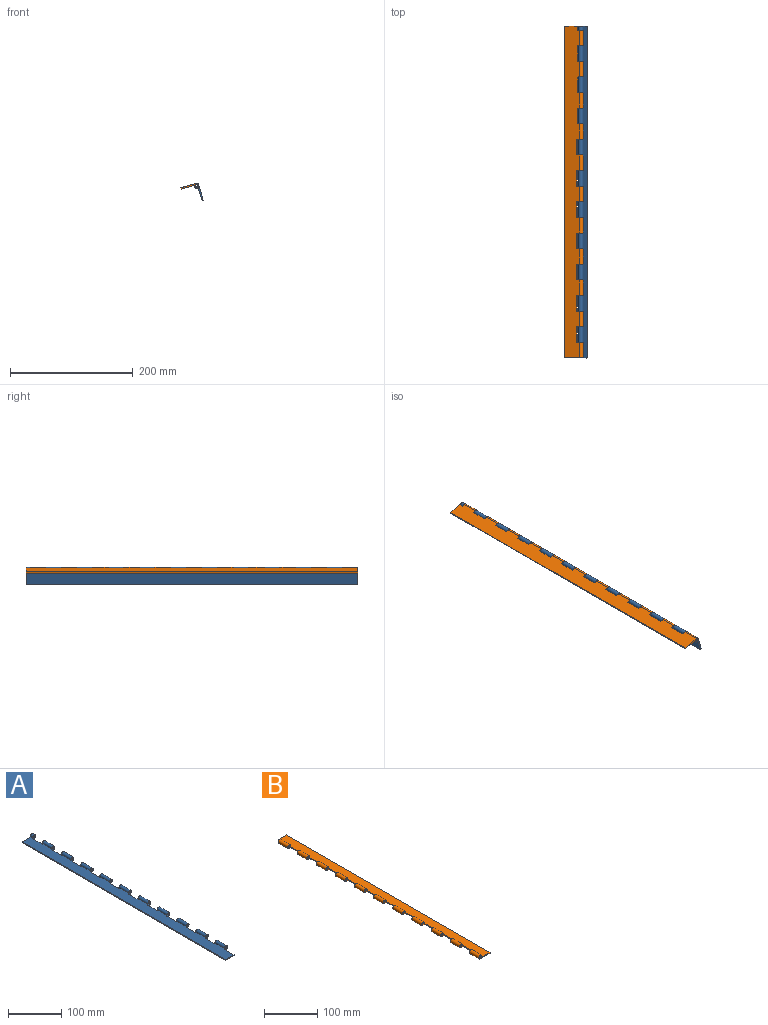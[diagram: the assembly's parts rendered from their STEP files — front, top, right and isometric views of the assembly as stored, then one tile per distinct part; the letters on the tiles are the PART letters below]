
ASSEMBLY  parts=2 mates=1
PART A: 71 faces, bbox 29.5x540x8 mm
  f0: plane 540x25.5mm, normal (0,0,1), area 12652.4mm2, adj f13,f14,f15,f16,f17,f18,f19,f20
  f1: plane 540x25.5mm, normal (0,0,-1), area 12652.4mm2, adj f24,f25,f26,f27,f28,f29,f30,f31
  f2: plane 6.6x2mm, normal (0,0,-1), area 13.2mm2, adj f13,f24,f38,f68
  f3: plane 25.4x2mm, normal (0,0,-1), area 50.8mm2, adj f14,f25,f66,f70
  f4: plane 25.4x2mm, normal (0,0,-1), area 50.8mm2, adj f15,f26,f63,f65
  f5: plane 25.4x2mm, normal (0,0,-1), area 50.8mm2, adj f16,f27,f60,f62
  f6: plane 25.4x2mm, normal (0,0,-1), area 50.8mm2, adj f17,f28,f57,f59
  f7: plane 25.4x2mm, normal (0,0,-1), area 50.8mm2, adj f18,f29,f54,f56
  f8: plane 25.4x2mm, normal (0,0,-1), area 50.8mm2, adj f19,f30,f48,f50
  f9: plane 25.4x2mm, normal (0,0,-1), area 50.8mm2, adj f20,f31,f51,f53
  f10: plane 25.4x2mm, normal (0,0,-1), area 50.8mm2, adj f21,f32,f45,f47
  f11: plane 25.4x2mm, normal (0,0,-1), area 50.8mm2, adj f22,f33,f42,f44
  f12: plane 25.4x2mm, normal (0,0,-1), area 50.8mm2, adj f23,f34,f39,f41
  f13: cylinder r=2mm len=6.6mm, axis (0,1,0), area 62.2mm2, adj f0,f2,f38,f68
  f14: cylinder r=2mm len=25.4mm, axis (0,1,0), area 239.4mm2, adj f0,f3,f66,f70
  f15: cylinder r=2mm len=25.4mm, axis (0,1,0), area 239.4mm2, adj f0,f4,f63,f65
  f16: cylinder r=2mm len=25.4mm, axis (0,1,0), area 239.4mm2, adj f0,f5,f60,f62
  f17: cylinder r=2mm len=25.4mm, axis (0,1,0), area 239.4mm2, adj f0,f6,f57,f59
  f18: cylinder r=2mm len=25.4mm, axis (0,1,0), area 239.4mm2, adj f0,f7,f54,f56
  f19: cylinder r=2mm len=25.4mm, axis (0,1,0), area 239.4mm2, adj f0,f8,f48,f50
  f20: cylinder r=2mm len=25.4mm, axis (0,1,0), area 239.4mm2, adj f0,f9,f51,f53
  f21: cylinder r=2mm len=25.4mm, axis (0,1,0), area 239.4mm2, adj f0,f10,f45,f47
  f22: cylinder r=2mm len=25.4mm, axis (0,1,0), area 239.4mm2, adj f0,f11,f42,f44
  f23: cylinder r=2mm len=25.4mm, axis (0,1,0), area 239.4mm2, adj f0,f12,f39,f41
  f24: cylinder r=4mm len=8mm, axis (0,1,0), area 124.4mm2, adj f1,f2,f38,f68
  f25: cylinder r=4mm len=25.4mm, axis (0,1,0), area 478.8mm2, adj f1,f3,f66,f70
  f26: cylinder r=4mm len=25.4mm, axis (0,1,0), area 478.8mm2, adj f1,f4,f63,f65
  f27: cylinder r=4mm len=25.4mm, axis (0,1,0), area 478.8mm2, adj f1,f5,f60,f62
  f28: cylinder r=4mm len=25.4mm, axis (0,1,0), area 478.8mm2, adj f1,f6,f57,f59
  f29: cylinder r=4mm len=25.4mm, axis (0,1,0), area 478.8mm2, adj f1,f7,f54,f56
  f30: cylinder r=4mm len=25.4mm, axis (0,1,0), area 478.8mm2, adj f1,f8,f48,f50
  f31: cylinder r=4mm len=25.4mm, axis (0,1,0), area 478.8mm2, adj f1,f9,f51,f53
  f32: cylinder r=4mm len=25.4mm, axis (0,1,0), area 478.8mm2, adj f1,f10,f45,f47
  f33: cylinder r=4mm len=25.4mm, axis (0,1,0), area 478.8mm2, adj f1,f11,f42,f44
  f34: cylinder r=4mm len=25.4mm, axis (0,1,0), area 478.8mm2, adj f1,f12,f39,f41
  f35: plane 21.5x2mm, normal (0,-1,0), area 43mm2, adj f0,f1,f37,f40
  f36: plane 25.5x2mm, normal (0,1,0), area 51mm2, adj f0,f1,f37,f38
  f37: plane 540x2mm, normal (-1,0,0), area 1080mm2, adj f0,f1,f35,f36
  f38: plane 8x8mm, normal (0,1,0), area 28.3mm2, adj f2,f13,f24,f36
  f39: plane 8x8mm, normal (0,-1,0), area 36.3mm2, adj f0,f1,f12,f23,f34,f40
  f40: plane 25.4x2mm, normal (1,0,0), area 50.8mm2, adj f0,f1,f35,f39
  f41: plane 8x8mm, normal (0,1,0), area 36.3mm2, adj f0,f1,f12,f23,f34,f43
  f42: plane 8x8mm, normal (0,-1,0), area 36.3mm2, adj f0,f1,f11,f22,f33,f43
  f43: plane 25.4x2mm, normal (1,0,0), area 50.8mm2, adj f0,f1,f41,f42
  f44: plane 8x8mm, normal (0,1,0), area 36.3mm2, adj f0,f1,f11,f22,f33,f46
  f45: plane 8x8mm, normal (0,-1,0), area 36.3mm2, adj f0,f1,f10,f21,f32,f46
  f46: plane 25.4x2mm, normal (1,0,0), area 50.8mm2, adj f0,f1,f44,f45
  f47: plane 8x8mm, normal (0,1,0), area 36.3mm2, adj f0,f1,f10,f21,f32,f49
  f48: plane 8x8mm, normal (0,-1,0), area 36.3mm2, adj f0,f1,f8,f19,f30,f49
  f49: plane 25.4x2mm, normal (1,0,0), area 50.8mm2, adj f0,f1,f47,f48
  f50: plane 8x8mm, normal (0,1,0), area 36.3mm2, adj f0,f1,f8,f19,f30,f52
  f51: plane 8x8mm, normal (0,-1,0), area 36.3mm2, adj f0,f1,f9,f20,f31,f52
  f52: plane 25.4x2mm, normal (1,0,0), area 50.8mm2, adj f0,f1,f50,f51
  f53: plane 8x8mm, normal (0,1,0), area 36.3mm2, adj f0,f1,f9,f20,f31,f55
  f54: plane 8x8mm, normal (0,-1,0), area 36.3mm2, adj f0,f1,f7,f18,f29,f55
  f55: plane 25.4x2mm, normal (1,0,0), area 50.8mm2, adj f0,f1,f53,f54
  f56: plane 8x8mm, normal (0,1,0), area 36.3mm2, adj f0,f1,f7,f18,f29,f58
  f57: plane 8x8mm, normal (0,-1,0), area 36.3mm2, adj f0,f1,f6,f17,f28,f58
  f58: plane 25.4x2mm, normal (1,0,0), area 50.8mm2, adj f0,f1,f56,f57
  f59: plane 8x8mm, normal (0,1,0), area 36.3mm2, adj f0,f1,f6,f17,f28,f61
  f60: plane 8x8mm, normal (0,-1,0), area 36.3mm2, adj f0,f1,f5,f16,f27,f61
  f61: plane 25.4x2mm, normal (1,0,0), area 50.8mm2, adj f0,f1,f59,f60
  f62: plane 8x8mm, normal (0,1,0), area 36.3mm2, adj f0,f1,f5,f16,f27,f64
  f63: plane 8x8mm, normal (0,-1,0), area 36.3mm2, adj f0,f1,f4,f15,f26,f64
  f64: plane 25.4x2mm, normal (1,0,0), area 50.8mm2, adj f0,f1,f62,f63
  f65: plane 8x8mm, normal (0,1,0), area 36.3mm2, adj f0,f1,f4,f15,f26,f67
  f66: plane 8x8mm, normal (0,-1,0), area 36.3mm2, adj f0,f1,f3,f14,f25,f67
  f67: plane 25.4x2mm, normal (1,0,0), area 50.8mm2, adj f0,f1,f65,f66
  f68: plane 8x8mm, normal (0,-1,0), area 36.3mm2, adj f0,f1,f2,f13,f24,f69
  f69: plane 25.4x2mm, normal (1,0,0), area 50.8mm2, adj f0,f1,f68,f70
  f70: plane 8x8mm, normal (0,1,0), area 36.3mm2, adj f0,f1,f3,f14,f25,f69
PART B: 71 faces, bbox 29.5x540x8 mm
  f0: plane 540x25.5mm, normal (0,0,1), area 12489.5mm2, adj f13,f14,f15,f16,f17,f18,f19,f20
  f1: plane 540x25.5mm, normal (0,0,-1), area 12489.5mm2, adj f24,f25,f26,f27,f28,f29,f30,f31
  f2: plane 25.4x2mm, normal (0,0,-1), area 50.8mm2, adj f13,f24,f40,f69
  f3: plane 25.4x2mm, normal (0,0,-1), area 50.8mm2, adj f14,f25,f65,f70
  f4: plane 25.4x2mm, normal (0,0,-1), area 50.8mm2, adj f15,f26,f62,f66
  f5: plane 25.4x2mm, normal (0,0,-1), area 50.8mm2, adj f16,f27,f59,f63
  f6: plane 25.4x2mm, normal (0,0,-1), area 50.8mm2, adj f17,f28,f56,f60
  f7: plane 25.4x2mm, normal (0,0,-1), area 50.8mm2, adj f18,f29,f53,f57
  f8: plane 25.4x2mm, normal (0,0,-1), area 50.8mm2, adj f19,f30,f50,f54
  f9: plane 25.4x2mm, normal (0,0,-1), area 50.8mm2, adj f20,f31,f47,f51
  f10: plane 25.4x2mm, normal (0,0,-1), area 50.8mm2, adj f21,f32,f44,f48
  f11: plane 25.4x2mm, normal (0,0,-1), area 50.8mm2, adj f22,f33,f42,f45
  f12: plane 25.4x2mm, normal (0,0,-1), area 50.8mm2, adj f23,f34,f38,f39
  f13: cylinder r=2mm len=25.4mm, axis (0,1,0), area 239.4mm2, adj f0,f2,f40,f69
  f14: cylinder r=2mm len=25.4mm, axis (0,1,0), area 239.4mm2, adj f0,f3,f65,f70
  f15: cylinder r=2mm len=25.4mm, axis (0,1,0), area 239.4mm2, adj f0,f4,f62,f66
  f16: cylinder r=2mm len=25.4mm, axis (0,1,0), area 239.4mm2, adj f0,f5,f59,f63
  f17: cylinder r=2mm len=25.4mm, axis (0,1,0), area 239.4mm2, adj f0,f6,f56,f60
  f18: cylinder r=2mm len=25.4mm, axis (0,1,0), area 239.4mm2, adj f0,f7,f53,f57
  f19: cylinder r=2mm len=25.4mm, axis (0,1,0), area 239.4mm2, adj f0,f8,f50,f54
  f20: cylinder r=2mm len=25.4mm, axis (0,1,0), area 239.4mm2, adj f0,f9,f47,f51
  f21: cylinder r=2mm len=25.4mm, axis (0,1,0), area 239.4mm2, adj f0,f10,f44,f48
  f22: cylinder r=2mm len=25.4mm, axis (0,1,0), area 239.4mm2, adj f0,f11,f42,f45
  f23: cylinder r=2mm len=25.4mm, axis (0,1,0), area 239.4mm2, adj f0,f12,f38,f39
  f24: cylinder r=4mm len=25.4mm, axis (0,1,0), area 478.8mm2, adj f1,f2,f40,f69
  f25: cylinder r=4mm len=25.4mm, axis (0,1,0), area 478.8mm2, adj f1,f3,f65,f70
  f26: cylinder r=4mm len=25.4mm, axis (0,1,0), area 478.8mm2, adj f1,f4,f62,f66
  f27: cylinder r=4mm len=25.4mm, axis (0,1,0), area 478.8mm2, adj f1,f5,f59,f63
  f28: cylinder r=4mm len=25.4mm, axis (0,1,0), area 478.8mm2, adj f1,f6,f56,f60
  f29: cylinder r=4mm len=25.4mm, axis (0,1,0), area 478.8mm2, adj f1,f7,f53,f57
  f30: cylinder r=4mm len=25.4mm, axis (0,1,0), area 478.8mm2, adj f1,f8,f50,f54
  f31: cylinder r=4mm len=25.4mm, axis (0,1,0), area 478.8mm2, adj f1,f9,f47,f51
  f32: cylinder r=4mm len=25.4mm, axis (0,1,0), area 478.8mm2, adj f1,f10,f44,f48
  f33: cylinder r=4mm len=25.4mm, axis (0,1,0), area 478.8mm2, adj f1,f11,f42,f45
  f34: cylinder r=4mm len=25.4mm, axis (0,1,0), area 478.8mm2, adj f1,f12,f38,f39
  f35: plane 25.5x2mm, normal (0,-1,0), area 51mm2, adj f0,f1,f36,f38
  f36: plane 540x2mm, normal (1,0,0), area 1080mm2, adj f0,f1,f35,f37
  f37: plane 21.5x2mm, normal (0,1,0), area 43mm2, adj f0,f1,f36,f43
  f38: plane 8x8mm, normal (0,-1,0), area 28.3mm2, adj f12,f23,f34,f35
  f39: plane 9.2x8mm, normal (0,1,0), area 38.7mm2, adj f0,f1,f12,f23,f34,f41
  f40: plane 9.2x8mm, normal (0,-1,0), area 38.7mm2, adj f0,f1,f2,f13,f24,f41
  f41: plane 25.4x2mm, normal (-1,0,0), area 50.8mm2, adj f0,f1,f39,f40
  f42: plane 8.03x8mm, normal (0,1,0), area 36.3mm2, adj f0,f1,f11,f22,f33,f43
  f43: plane 6.6x2mm, normal (-1,0,0), area 13.2mm2, adj f0,f1,f37,f42
  f44: plane 8.26x8mm, normal (0,1,0), area 36.8mm2, adj f0,f1,f10,f21,f32,f46
  f45: plane 8.15x8mm, normal (0,-1,0), area 36.6mm2, adj f0,f1,f11,f22,f33,f46
  f46: plane 25.4x2mm, normal (-1,0,0), area 50.8mm2, adj f0,f1,f44,f45
  f47: plane 8.5x8mm, normal (0,1,0), area 37.3mm2, adj f0,f1,f9,f20,f31,f49
  f48: plane 8.38x8mm, normal (0,-1,0), area 37mm2, adj f0,f1,f10,f21,f32,f49
  f49: plane 25.4x2mm, normal (-1,0,0), area 50.8mm2, adj f0,f1,f47,f48
  f50: plane 8.73x8mm, normal (0,1,0), area 37.7mm2, adj f0,f1,f8,f19,f30,f52
  f51: plane 8.62x8mm, normal (0,-1,0), area 37.5mm2, adj f0,f1,f9,f20,f31,f52
  f52: plane 25.4x2mm, normal (-1,0,0), area 50.8mm2, adj f0,f1,f50,f51
  f53: plane 8.97x8mm, normal (0,1,0), area 38.2mm2, adj f0,f1,f7,f18,f29,f55
  f54: plane 8.85x8mm, normal (0,-1,0), area 38mm2, adj f0,f1,f8,f19,f30,f55
  f55: plane 25.4x2mm, normal (-1,0,0), area 50.8mm2, adj f0,f1,f53,f54
  f56: plane 9.2x8mm, normal (0,1,0), area 38.7mm2, adj f0,f1,f6,f17,f28,f58
  f57: plane 9.08x8mm, normal (0,-1,0), area 38.4mm2, adj f0,f1,f7,f18,f29,f58
  f58: plane 25.4x2mm, normal (-1,0,0), area 50.8mm2, adj f0,f1,f56,f57
  f59: plane 9.2x8mm, normal (0,1,0), area 38.7mm2, adj f0,f1,f5,f16,f27,f61
  f60: plane 9.2x8mm, normal (0,-1,0), area 38.7mm2, adj f0,f1,f6,f17,f28,f61
  f61: plane 25.4x2mm, normal (-1,0,0), area 50.8mm2, adj f0,f1,f59,f60
  f62: plane 9.2x8mm, normal (0,1,0), area 38.7mm2, adj f0,f1,f4,f15,f26,f64
  f63: plane 9.2x8mm, normal (0,-1,0), area 38.7mm2, adj f0,f1,f5,f16,f27,f64
  f64: plane 25.4x2mm, normal (-1,0,0), area 50.8mm2, adj f0,f1,f62,f63
  f65: plane 9.2x8mm, normal (0,1,0), area 38.7mm2, adj f0,f1,f3,f14,f25,f67
  f66: plane 9.2x8mm, normal (0,-1,0), area 38.7mm2, adj f0,f1,f4,f15,f26,f67
  f67: plane 25.4x2mm, normal (-1,0,0), area 50.8mm2, adj f0,f1,f65,f66
  f68: plane 25.4x2mm, normal (-1,0,0), area 50.8mm2, adj f0,f1,f69,f70
  f69: plane 9.2x8mm, normal (0,1,0), area 38.7mm2, adj f0,f1,f2,f13,f24,f68
  f70: plane 9.2x8mm, normal (0,-1,0), area 38.7mm2, adj f0,f1,f3,f14,f25,f68
PLACE A rot(axis=(0,-1,0),106.2deg) t=(8.44,-280.72,0.53)mm
PLACE B rot(axis=(0,1,0),163.8deg) t=(5.97,-280.72,1.89)mm
MATE revolute B.f13 <-> A.f13  axis (0,1,0) through (6.52,252.68,-0.03)mm
